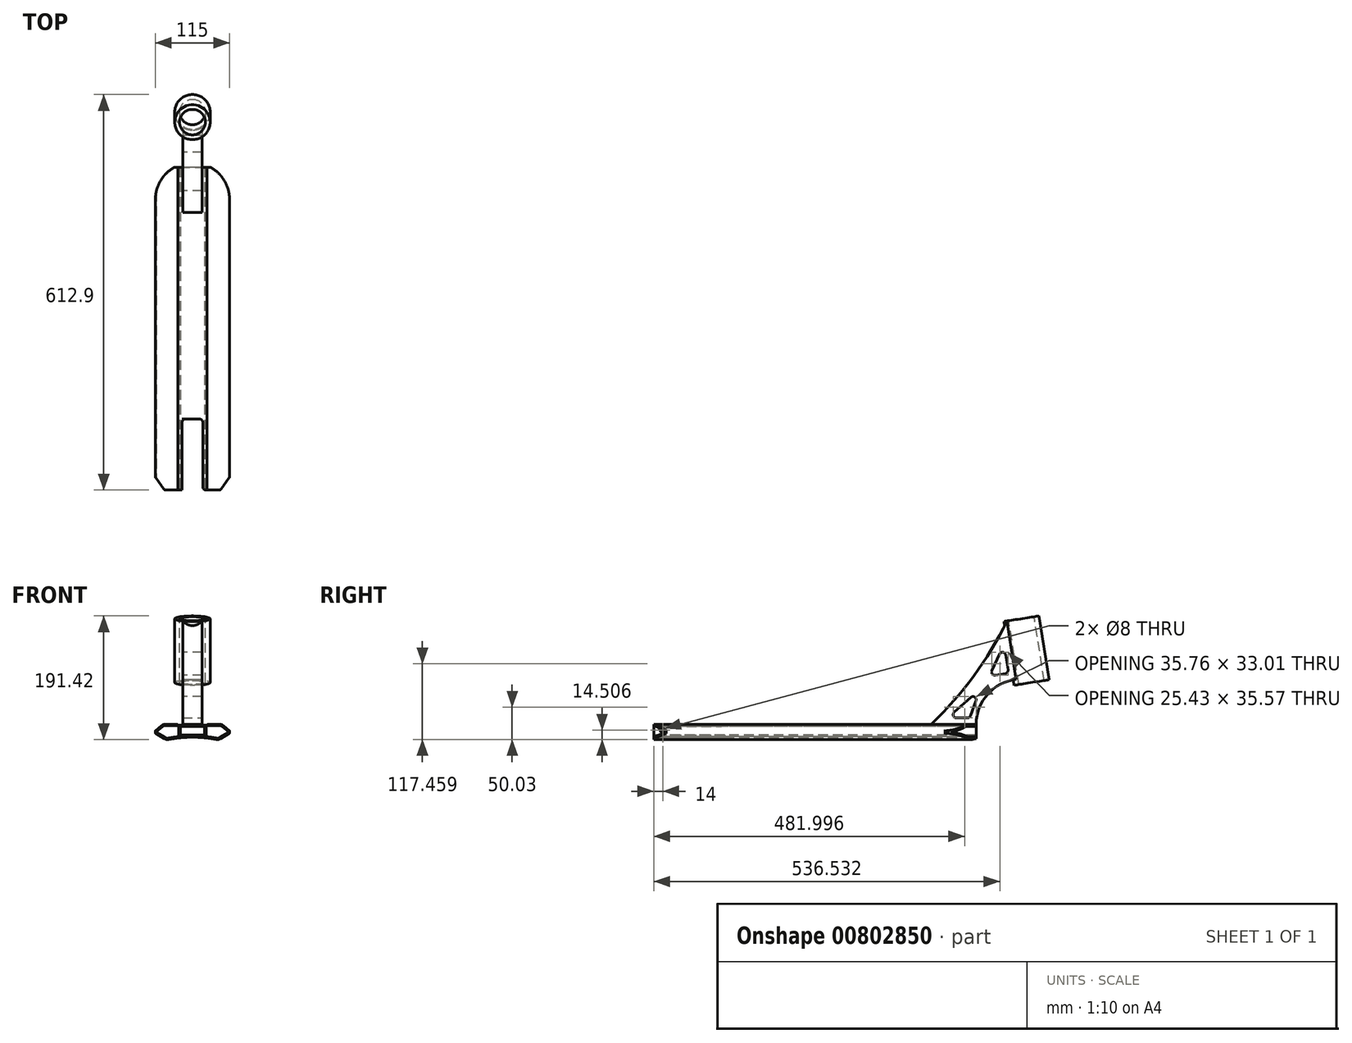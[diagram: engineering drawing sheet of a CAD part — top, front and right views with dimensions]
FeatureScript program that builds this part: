
annotation { "Feature Type Name" : "Feature", "Feature Type Description" : "" }
export const myFeature = defineFeature(function(context is Context, id is Id, definition is map)
    precondition{}
    {
        {
            var Q0;
            Q0=qCreatedBy(makeId("Front.planeOp"),FACE);
            var sketch = newSketch(context, id + "F0", { "sketchPlane" : qUnion([Q0])});
            skLineSegment(sketch, "E0", {"start": v(0, 0) * mm, "end": v(0, 71.95) * mm, "construction": true});
            skLineSegment(sketch, "E1", {"start": v(0, 25.77) * mm, "end": v(22.5, 25.77) * mm});
            skLineSegment(sketch, "E2", {"start": v(22.5, 25.77) * mm, "end": v(22.5, 27.07) * mm});
            skLineSegment(sketch, "E3", {"start": v(22.5, 27.07) * mm, "end": v(45.58, 27.07) * mm});
            skLineSegment(sketch, "E4", {"start": v(45.58, 27.07) * mm, "end": v(57.5, 17.07) * mm});
            skLineSegment(sketch, "E5", {"start": v(57.5, 17.07) * mm, "end": v(57.5, 13.07) * mm});
            skLineSegment(sketch, "E6", {"start": v(57.5, 13.07) * mm, "end": v(40.18, 3.07) * mm});
            skLineSegment(sketch, "E7.MirrorCS", {"start": v(0, 25.77) * mm, "end": v(-22.5, 25.77) * mm});
            skLineSegment(sketch, "E8.MirrorCS", {"start": v(-22.5, 27.07) * mm, "end": v(-45.58, 27.07) * mm});
            skLineSegment(sketch, "E9.MirrorCS", {"start": v(-22.5, 25.77) * mm, "end": v(-22.5, 27.07) * mm});
            skLineSegment(sketch, "E10.MirrorCS", {"start": v(-45.58, 27.07) * mm, "end": v(-57.5, 17.07) * mm});
            skLineSegment(sketch, "E11.MirrorCS", {"start": v(-57.5, 17.07) * mm, "end": v(-57.5, 13.07) * mm});
            skLineSegment(sketch, "E12.MirrorCS", {"start": v(-57.5, 13.07) * mm, "end": v(-40.18, 3.07) * mm});
            skArc(sketch, "E13", {"start": v(40.18, 3.07) * mm, "mid": v(0, 7.15) * mm, "end": v(-40.18, 3.07) * mm});
            skSolve(sketch);
        }
        {
            var Q0;
            Q0=qSketchRegion(id+"F0",true);
            extrude(context, id + "F1", {"entities" : qUnion([Q0]), "endBound" : BoundingType.SYMMETRIC, "depth" : 500 * mm, "offsetDistance" : 25 * mm});
        }
        {
            var Q0;
            Q0=qCreatedBy(makeId("Front.planeOp"),FACE);
            var sketch = newSketch(context, id + "F2", { "sketchPlane" : qUnion([Q0])});
            skLineSegment(sketch, "E14.bottom", {"start": v(-19, 23.77) * mm, "end": v(19, 23.77) * mm});
            skLineSegment(sketch, "E14.top", {"start": v(-19, 10.77) * mm, "end": v(19, 10.77) * mm});
            skLineSegment(sketch, "E14.left", {"start": v(-19, 23.77) * mm, "end": v(-19, 10.77) * mm});
            skLineSegment(sketch, "E14.right", {"start": v(19, 23.77) * mm, "end": v(19, 10.77) * mm});
            skSolve(sketch);
        }
        {
            var Q0;
            Q0=qSketchRegion(id+"F2",true);
            extrude(context, id + "F3", {"entities" : qUnion([Q0]), "operationType" : NewBodyOperationType.REMOVE, "endBound" : BoundingType.SYMMETRIC, "oppositeDirection" : true, "depth" : 500 * mm, "offsetDistance" : 25 * mm});
        }
        {
            var Q0;
            Q0=makeQuery(id+"F1.opExtrude","SWEPT_EDGE",EDGE,{"disambiguationData":[OSD([sQuery(id+"F0.wireOp",EDGE,"E8.MirrorCS"),sQuery(id+"F0.wireOp",EDGE,"E9.MirrorCS")])]});
            var Q1;
            Q1=makeQuery(id+"F1.opExtrude","SWEPT_EDGE",EDGE,{"disambiguationData":[OSD([sQuery(id+"F0.wireOp",EDGE,"E2"),sQuery(id+"F0.wireOp",EDGE,"E3")])]});
            fillet(context, id + "F4", {"entities" : qUnion([Q0, Q1]), "radius" : 2 * mm, "tangentPropagation" : true, "allowEdgeOverflow" : false});
        }
        {
            var Q0;
            Q0=makeQuery(id+"F1.opExtrude","SWEPT_EDGE",EDGE,{"disambiguationData":[OSD([sQuery(id+"F0.wireOp",EDGE,"E8.MirrorCS"),sQuery(id+"F0.wireOp",EDGE,"E10.MirrorCS")])]});
            var Q1;
            Q1=makeQuery(id+"F1.opExtrude","SWEPT_EDGE",EDGE,{"disambiguationData":[OSD([sQuery(id+"F0.wireOp",EDGE,"E3"),sQuery(id+"F0.wireOp",EDGE,"E4")])]});
            var Q2;
            Q2=makeQuery(id+"F1.opExtrude","SWEPT_EDGE",EDGE,{"disambiguationData":[OSD([sQuery(id+"F0.wireOp",EDGE,"E6"),sQuery(id+"F0.wireOp",EDGE,"E13")])]});
            var Q3;
            Q3=makeQuery(id+"F1.opExtrude","SWEPT_EDGE",EDGE,{"disambiguationData":[OSD([sQuery(id+"F0.wireOp",EDGE,"E12.MirrorCS"),sQuery(id+"F0.wireOp",EDGE,"E13")])]});
            fillet(context, id + "F5", {"entities" : qUnion([Q0, Q1, Q2, Q3]), "radius" : 9 * mm, "tangentPropagation" : true, "allowEdgeOverflow" : false});
        }
        {
            var Q0;
            Q0=makeQuery(id+"F1.opExtrude","SWEPT_EDGE",EDGE,{"disambiguationData":[OSD([sQuery(id+"F0.wireOp",EDGE,"E4"),sQuery(id+"F0.wireOp",EDGE,"E5")])]});
            var Q1;
            Q1=makeQuery(id+"F1.opExtrude","SWEPT_EDGE",EDGE,{"disambiguationData":[OSD([sQuery(id+"F0.wireOp",EDGE,"E5"),sQuery(id+"F0.wireOp",EDGE,"E6")])]});
            var Q2;
            Q2=makeQuery(id+"F1.opExtrude","SWEPT_EDGE",EDGE,{"disambiguationData":[OSD([sQuery(id+"F0.wireOp",EDGE,"E10.MirrorCS"),sQuery(id+"F0.wireOp",EDGE,"E11.MirrorCS")])]});
            var Q3;
            Q3=makeQuery(id+"F1.opExtrude","SWEPT_EDGE",EDGE,{"disambiguationData":[OSD([sQuery(id+"F0.wireOp",EDGE,"E11.MirrorCS"),sQuery(id+"F0.wireOp",EDGE,"E12.MirrorCS")])]});
            fillet(context, id + "F6", {"entities" : qUnion([Q0, Q1, Q2, Q3]), "radius" : 1 * mm, "tangentPropagation" : true, "allowEdgeOverflow" : false});
        }
        {
            var Q0;
            Q0=makeQuery(id+"F1.opExtrude","CAP_FACE",FACE,{"disambiguationData":[OSD([sQuery(id+"F0.wireOp",EDGE,"E1"),sQuery(id+"F0.wireOp",EDGE,"E2"),sQuery(id+"F0.wireOp",EDGE,"E3"),sQuery(id+"F0.wireOp",EDGE,"E4"),sQuery(id+"F0.wireOp",EDGE,"E5"),sQuery(id+"F0.wireOp",EDGE,"E6"),sQuery(id+"F0.wireOp",EDGE,"E7.MirrorCS"),sQuery(id+"F0.wireOp",EDGE,"E8.MirrorCS"),sQuery(id+"F0.wireOp",EDGE,"E9.MirrorCS"),sQuery(id+"F0.wireOp",EDGE,"E10.MirrorCS"),sQuery(id+"F0.wireOp",EDGE,"E11.MirrorCS"),sQuery(id+"F0.wireOp",EDGE,"E12.MirrorCS"),sQuery(id+"F0.wireOp",EDGE,"E13")])],"isStart":false});
            var sketch = newSketch(context, id + "F7", { "sketchPlane" : qUnion([Q0])});
            skArc(sketch, "E15.0", {"start": v(-21, 8.06) * mm, "mid": v(-29.18, 7.03) * mm, "end": v(-37.3, 5.68) * mm});
            skArc(sketch, "E15.1", {"start": v(-42.1, 6.5) * mm, "mid": v(-39.78, 5.65) * mm, "end": v(-37.3, 5.68) * mm});
            skLineSegment(sketch, "E15.2", {"start": v(-24.37, 25.07) * mm, "end": v(-42.3, 25.07) * mm});
            skArc(sketch, "E15.3", {"start": v(-42.3, 25.07) * mm, "mid": v(-44.7, 24.65) * mm, "end": v(-46.8, 23.44) * mm});
            skLineSegment(sketch, "E15.4", {"start": v(-46.8, 23.44) * mm, "end": v(-55.76, 15.93) * mm});
            skLineSegment(sketch, "E15.5", {"start": v(-55.61, 14.3) * mm, "end": v(-42.1, 6.5) * mm});
            skLineSegment(sketch, "E16.0", {"start": v(-21, 23.77) * mm, "end": v(-21, 10.77) * mm});
            skLineSegment(sketch, "E17.0", {"start": v(-22.5, 23.77) * mm, "end": v(-21, 23.77) * mm});
            skPoint(sketch, "E18.visualSharp", {"position": v(-56.85, 15) * mm});
            skArc(sketch, "E18.filletArc", {"start": v(-55.76, 15.93) * mm, "mid": v(-56.1, 15.07) * mm, "end": v(-55.61, 14.3) * mm});
            skArc(sketch, "E19", {"start": v(-24.37, 25.07) * mm, "mid": v(-23.23, 24.72) * mm, "end": v(-22.5, 23.77) * mm});
            skLineSegment(sketch, "E20", {"start": v(-21, 10.77) * mm, "end": v(-21, 8.06) * mm});
            skLineSegment(sketch, "E21.MirrorCS", {"start": v(24.37, 25.07) * mm, "end": v(42.3, 25.07) * mm});
            skArc(sketch, "E22.MirrorCS", {"start": v(24.37, 25.07) * mm, "mid": v(23.23, 24.72) * mm, "end": v(22.5, 23.77) * mm});
            skLineSegment(sketch, "E23.MirrorCS", {"start": v(22.5, 23.77) * mm, "end": v(21, 23.77) * mm});
            skLineSegment(sketch, "E24.MirrorCS", {"start": v(21, 23.77) * mm, "end": v(21, 10.77) * mm});
            skArc(sketch, "E25.MirrorCS", {"start": v(21, 8.06) * mm, "mid": v(29.18, 7.03) * mm, "end": v(37.3, 5.68) * mm});
            skArc(sketch, "E26.MirrorCS", {"start": v(42.1, 6.5) * mm, "mid": v(39.78, 5.65) * mm, "end": v(37.3, 5.68) * mm});
            skLineSegment(sketch, "E27.MirrorCS", {"start": v(21, 10.77) * mm, "end": v(21, 8.06) * mm});
            skLineSegment(sketch, "E28.MirrorCS", {"start": v(55.61, 14.3) * mm, "end": v(42.1, 6.5) * mm});
            skLineSegment(sketch, "E29.MirrorCS", {"start": v(46.8, 23.44) * mm, "end": v(55.76, 15.93) * mm});
            skArc(sketch, "E30.MirrorCS", {"start": v(42.3, 25.07) * mm, "mid": v(44.7, 24.65) * mm, "end": v(46.8, 23.44) * mm});
            skArc(sketch, "E31.MirrorCS", {"start": v(55.76, 15.93) * mm, "mid": v(56.1, 15.07) * mm, "end": v(55.61, 14.3) * mm});
            skSolve(sketch);
        }
        {
            var Q0;
            Q0=makeQuery(id+"F7.imprint","IMPRINT",FACE,{"disambiguationData":[TD([[makeQuery(id+"F7.imprint","IMPRINT",EDGE,{"derivedFrom":sQuery(id+"F7.wireOp",EDGE,"E15.0")}),-1.0]])]});
            var Q1;
            Q1=makeQuery(id+"F7.imprint","IMPRINT",FACE,{"disambiguationData":[TD([[makeQuery(id+"F7.imprint","IMPRINT",EDGE,{"derivedFrom":sQuery(id+"F7.wireOp",EDGE,"E21.MirrorCS")}),-1.0]])]});
            extrude(context, id + "F8", {"entities" : qUnion([Q0, Q1]), "operationType" : NewBodyOperationType.REMOVE, "endBound" : BoundingType.THROUGH_ALL, "oppositeDirection" : true, "depth" : 25 * mm, "offsetDistance" : 25 * mm});
        }
        {
            var Q0;
            Q0=qCreatedBy(makeId("Top.planeOp"),FACE);
            var sketch = newSketch(context, id + "F9", { "sketchPlane" : qUnion([Q0])});
            skArc(sketch, "E32", {"start": v(57.5, 200) * mm, "mid": v(0, 257.5) * mm, "end": v(-57.5, 200) * mm});
            skLineSegment(sketch, "E33", {"start": v(-57.5, 280) * mm, "end": v(-57.5, 200) * mm});
            skLineSegment(sketch, "E34", {"start": v(57.5, 200) * mm, "end": v(57.5, 280) * mm});
            skLineSegment(sketch, "E35", {"start": v(-57.5, 280) * mm, "end": v(57.5, 280) * mm});
            skSolve(sketch);
        }
        {
            var Q0;
            Q0=qSketchRegion(id+"F9",true);
            extrude(context, id + "F10", {"entities" : qUnion([Q0]), "operationType" : NewBodyOperationType.REMOVE, "endBound" : BoundingType.THROUGH_ALL, "oppositeDirection" : true, "depth" : 25 * mm, "offsetDistance" : 25 * mm, "hasSecondDirection" : true, "secondDirectionBound" : SecondDirectionBoundingType.THROUGH_ALL, "secondDirectionOppositeDirection" : false, "secondDirectionDepth" : 25 * mm});
        }
        {
            var Q0;
            Q0=qCreatedBy(makeId("Top.planeOp"),FACE);
            var sketch = newSketch(context, id + "F11", { "sketchPlane" : qUnion([Q0])});
            skLineSegment(sketch, "E36", {"start": v(-68, -216) * mm, "end": v(-68, -346) * mm});
            skLineSegment(sketch, "E37", {"start": v(-68, -346) * mm, "end": v(68, -346) * mm});
            skLineSegment(sketch, "E38", {"start": v(68, -346) * mm, "end": v(68, -216) * mm});
            skLineSegment(sketch, "E39", {"start": v(68, -216) * mm, "end": v(43.3, -250) * mm});
            skLineSegment(sketch, "E40", {"start": v(43.3, -250) * mm, "end": v(16, -250) * mm});
            skLineSegment(sketch, "E41", {"start": v(16, -250) * mm, "end": v(16, -140) * mm});
            skLineSegment(sketch, "E42", {"start": v(16, -140) * mm, "end": v(-16, -140) * mm});
            skLineSegment(sketch, "E43", {"start": v(-16, -140) * mm, "end": v(-16, -250) * mm});
            skLineSegment(sketch, "E44", {"start": v(-16, -250) * mm, "end": v(-43.3, -250) * mm});
            skLineSegment(sketch, "E45", {"start": v(-43.3, -250) * mm, "end": v(-68, -216) * mm});
            skSolve(sketch);
        }
        {
            var Q0;
            Q0=qSketchRegion(id+"F11",true);
            extrude(context, id + "F12", {"entities" : qUnion([Q0]), "operationType" : NewBodyOperationType.REMOVE, "endBound" : BoundingType.THROUGH_ALL, "depth" : 25 * mm, "offsetDistance" : 25 * mm, "hasSecondDirection" : true, "secondDirectionBound" : SecondDirectionBoundingType.THROUGH_ALL, "secondDirectionOppositeDirection" : true, "secondDirectionDepth" : 25 * mm});
        }
        {
            var Q0;
            {var subQ0=sQuery(id+"F0.wireOp",EDGE,"E13");var subQ1=sQuery(id+"F11.wireOp",EDGE,"E43");Q0=makeQuery(id+"F12.boolean.opBoolean","COPY",EDGE,{"disambiguationData":[TD([makeQuery(id+"F1.opExtrude","SWEPT_FACE",FACE,{"disambiguationData":[OSD([subQ0])]})])],"derivedFrom":makeQuery(id+"F12.opExtrude","SWEPT_EDGE",EDGE,{"disambiguationData":[OSD([subQ1,sQuery(id+"F11.wireOp",EDGE,"E44")])]})});}
            var Q1;
            {var subQ2=sQuery(id+"F11.wireOp",EDGE,"E43");Q1=makeQuery(id+"F12.boolean.opBoolean","COPY",EDGE,{"disambiguationData":[TD([makeQuery(id+"F3.boolean.opBoolean","COPY",FACE,{"derivedFrom":makeQuery(id+"F3.opExtrude","SWEPT_FACE",FACE,{"disambiguationData":[OSD([sQuery(id+"F2.wireOp",EDGE,"E14.bottom")])]})})])],"derivedFrom":makeQuery(id+"F12.opExtrude","SWEPT_EDGE",EDGE,{"disambiguationData":[OSD([subQ2,sQuery(id+"F11.wireOp",EDGE,"E44")])]})});}
            var Q2;
            {var subQ0=sQuery(id+"F11.wireOp",EDGE,"E42");var subQ1=sQuery(id+"F11.wireOp",EDGE,"E43");Q2=makeQuery(id+"F12.boolean.opBoolean","COPY",EDGE,{"disambiguationData":[TD([makeQuery(id+"F3.boolean.opBoolean","COPY",FACE,{"derivedFrom":makeQuery(id+"F3.opExtrude","SWEPT_FACE",FACE,{"disambiguationData":[OSD([sQuery(id+"F2.wireOp",EDGE,"E14.bottom")])]})})])],"derivedFrom":makeQuery(id+"F12.opExtrude","SWEPT_EDGE",EDGE,{"disambiguationData":[OSD([subQ0,subQ1])]})});}
            var Q3;
            {var subQ0=sQuery(id+"F11.wireOp",EDGE,"E41");var subQ1=sQuery(id+"F11.wireOp",EDGE,"E42");Q3=makeQuery(id+"F12.boolean.opBoolean","COPY",EDGE,{"disambiguationData":[TD([makeQuery(id+"F1.opExtrude","SWEPT_FACE",FACE,{"disambiguationData":[OSD([sQuery(id+"F0.wireOp",EDGE,"E13")])]})])],"derivedFrom":makeQuery(id+"F12.opExtrude","SWEPT_EDGE",EDGE,{"disambiguationData":[OSD([subQ0,subQ1])]})});}
            var Q4;
            {var subQ0=sQuery(id+"F0.wireOp",EDGE,"E13");var subQ1=sQuery(id+"F11.wireOp",EDGE,"E41");Q4=makeQuery(id+"F12.boolean.opBoolean","COPY",EDGE,{"disambiguationData":[TD([makeQuery(id+"F1.opExtrude","SWEPT_FACE",FACE,{"disambiguationData":[OSD([subQ0])]})])],"derivedFrom":makeQuery(id+"F12.opExtrude","SWEPT_EDGE",EDGE,{"disambiguationData":[OSD([sQuery(id+"F11.wireOp",EDGE,"E40"),subQ1])]})});}
            var Q5;
            {var subQ2=sQuery(id+"F11.wireOp",EDGE,"E41");Q5=makeQuery(id+"F12.boolean.opBoolean","COPY",EDGE,{"disambiguationData":[TD([makeQuery(id+"F3.boolean.opBoolean","COPY",FACE,{"derivedFrom":makeQuery(id+"F3.opExtrude","SWEPT_FACE",FACE,{"disambiguationData":[OSD([sQuery(id+"F2.wireOp",EDGE,"E14.bottom")])]})})])],"derivedFrom":makeQuery(id+"F12.opExtrude","SWEPT_EDGE",EDGE,{"disambiguationData":[OSD([sQuery(id+"F11.wireOp",EDGE,"E40"),subQ2])]})});}
            var Q6;
            {var subQ0=sQuery(id+"F11.wireOp",EDGE,"E42");var subQ1=sQuery(id+"F11.wireOp",EDGE,"E41");Q6=makeQuery(id+"F12.boolean.opBoolean","COPY",EDGE,{"disambiguationData":[TD([makeQuery(id+"F3.boolean.opBoolean","COPY",FACE,{"derivedFrom":makeQuery(id+"F3.opExtrude","SWEPT_FACE",FACE,{"disambiguationData":[OSD([sQuery(id+"F2.wireOp",EDGE,"E14.bottom")])]})})])],"derivedFrom":makeQuery(id+"F12.opExtrude","SWEPT_EDGE",EDGE,{"disambiguationData":[OSD([subQ1,subQ0])]})});}
            fillet(context, id + "F13", {"entities" : qUnion([Q0, Q1, Q2, Q3, Q4, Q5, Q6]), "radius" : 5 * mm, "tangentPropagation" : true, "allowEdgeOverflow" : false});
        }
        {
            var Q0;
            Q0=qCreatedBy(makeId("Right.planeOp"),FACE);
            var sketch = newSketch(context, id + "F14", { "sketchPlane" : qUnion([Q0])});
            skLineSegment(sketch, "E46", {"start": v(250, 27.07) * mm, "end": v(180, 27.07) * mm});
            skArc(sketch, "E47", {"start": v(311.71, 96.58) * mm, "mid": v(267.66, 73.55) * mm, "end": v(250, 27.07) * mm});
            skArc(sketch, "E48", {"start": v(180, 27.07) * mm, "mid": v(245.97, 101.74) * mm, "end": v(297.38, 187.07) * mm});
            skLineSegment(sketch, "E49", {"start": v(297.38, 187.07) * mm, "end": v(342.82, 194.27) * mm});
            skLineSegment(sketch, "E50", {"start": v(342.82, 194.27) * mm, "end": v(358.46, 95.5) * mm});
            skLineSegment(sketch, "E51", {"start": v(358.46, 95.5) * mm, "end": v(313.03, 88.3) * mm});
            skLineSegment(sketch, "E52", {"start": v(313.03, 88.3) * mm, "end": v(311.71, 96.58) * mm});
            skSolve(sketch);
        }
        {
            var Q0;
            Q0=qSketchRegion(id+"F14",true);
            extrude(context, id + "F15", {"entities" : qUnion([Q0]), "endBound" : BoundingType.SYMMETRIC, "depth" : 30 * mm, "offsetDistance" : 25 * mm});
        }
        {
            var Q0;
            Q0=makeQuery(id+"F15.opExtrude","SWEPT_FACE",FACE,{"disambiguationData":[OSD([sQuery(id+"F14.wireOp",EDGE,"E49")])]});
            var sketch = newSketch(context, id + "F16", { "sketchPlane" : qUnion([Q0])});
            skCircle(sketch, "E53", {"center": v(0, 345.99) * mm, "radius": 27.5 * mm});
            skPoint(sketch, "E53.centerSnap0", {"position": v(15, 345.99) * mm});
            skSolve(sketch);
        }
        {
            var Q0;
            Q0=qSketchRegion(id+"F16",true);
            var Q1;
            Q1=makeQuery(id+"F15.opExtrude","SWEPT_FACE",FACE,{"disambiguationData":[OSD([sQuery(id+"F14.wireOp",EDGE,"E51")])]});
            extrude(context, id + "F17", {"entities" : qUnion([Q0]), "operationType" : NewBodyOperationType.ADD, "endBound" : BoundingType.UP_TO_SURFACE, "oppositeDirection" : true, "depth" : 25 * mm, "endBoundEntityFace" : qUnion([Q1]), "offsetDistance" : 25 * mm});
        }
        {
            var Q0;
            Q0=makeQuery(id+"F17.boolean.opBoolean","MERGE",FACE,{"derivedFrom":[makeQuery(id+"F15.opExtrude","SWEPT_FACE",FACE,{"disambiguationData":[OSD([sQuery(id+"F14.wireOp",EDGE,"E49")])]}),makeQuery(id+"F17.opExtrude","CAP_FACE",FACE,{"disambiguationData":[OSD([sQuery(id+"F16.wireOp",EDGE,"E53")])],"isStart":true})]});
            var sketch = newSketch(context, id + "F18", { "sketchPlane" : qUnion([Q0])});
            skPoint(sketch, "E54", {"position": v(0, 345.99) * mm});
            skSolve(sketch);
        }
        {
            var Q0;
            Q0=sQuery(id+"F18.wireOp",VERTEX,"E54");
            var Q1;
            Q1=makeQuery(id+"F15.opExtrude","SWEPT_BODY",BODY,{"disambiguationData":[OSD([sQuery(id+"F14.wireOp",EDGE,"E46"),sQuery(id+"F14.wireOp",EDGE,"E47"),sQuery(id+"F14.wireOp",EDGE,"E48"),sQuery(id+"F14.wireOp",EDGE,"E49"),sQuery(id+"F14.wireOp",EDGE,"E50"),sQuery(id+"F14.wireOp",EDGE,"E51"),sQuery(id+"F14.wireOp",EDGE,"E52")])]});
            hole(context, id + "F19", {"style" : HoleStyle.SIMPLE, "endStyle" : HoleEndStyle.THROUGH, "holeDiameter" : 40 * mm, "majorDiameter" : 5 * mm, "isTappedThrough" : true, "tappedDepth" : 12 * mm, "tapClearance" : 3, "locations" : qUnion([Q0]), "scope" : qUnion([Q1])});
        }
        {
            var Q0;
            Q0=makeQuery(id+"F8.boolean.opBoolean","COPY",FACE,{"derivedFrom":makeQuery(id+"F8.opExtrude","SWEPT_FACE",FACE,{"disambiguationData":[OSD([sQuery(id+"F7.wireOp",EDGE,"E24.MirrorCS"),sQuery(id+"F7.wireOp",EDGE,"E27.MirrorCS")])]})});
            var sketch = newSketch(context, id + "F20", { "sketchPlane" : qUnion([Q0])});
            skPoint(sketch, "E55", {"position": v(-236, 18.06) * mm});
            skSolve(sketch);
        }
        {
            var Q0;
            Q0=sQuery(id+"F20.wireOp",VERTEX,"E55");
            var Q1;
            Q1=makeQuery(id+"F1.opExtrude","SWEPT_BODY",BODY,{"disambiguationData":[OSD([sQuery(id+"F0.wireOp",EDGE,"E1"),sQuery(id+"F0.wireOp",EDGE,"E2"),sQuery(id+"F0.wireOp",EDGE,"E3"),sQuery(id+"F0.wireOp",EDGE,"E4"),sQuery(id+"F0.wireOp",EDGE,"E5"),sQuery(id+"F0.wireOp",EDGE,"E6"),sQuery(id+"F0.wireOp",EDGE,"E7.MirrorCS"),sQuery(id+"F0.wireOp",EDGE,"E8.MirrorCS"),sQuery(id+"F0.wireOp",EDGE,"E9.MirrorCS"),sQuery(id+"F0.wireOp",EDGE,"E10.MirrorCS"),sQuery(id+"F0.wireOp",EDGE,"E11.MirrorCS"),sQuery(id+"F0.wireOp",EDGE,"E12.MirrorCS"),sQuery(id+"F0.wireOp",EDGE,"E13")])]});
            hole(context, id + "F21", {"style" : HoleStyle.SIMPLE, "endStyle" : HoleEndStyle.BLIND, "holeDiameter" : 8 * mm, "majorDiameter" : 5 * mm, "holeDepth" : 66 * mm, "isTappedThrough" : true, "tappedDepth" : 12 * mm, "tapClearance" : 3, "locations" : qUnion([Q0]), "scope" : qUnion([Q1])});
        }
        {
            var Q0;
            Q0=makeQuery(id+"F15.opExtrude","CAP_FACE",FACE,{"disambiguationData":[OSD([sQuery(id+"F14.wireOp",EDGE,"E46"),sQuery(id+"F14.wireOp",EDGE,"E47"),sQuery(id+"F14.wireOp",EDGE,"E48"),sQuery(id+"F14.wireOp",EDGE,"E49"),sQuery(id+"F14.wireOp",EDGE,"E50"),sQuery(id+"F14.wireOp",EDGE,"E51"),sQuery(id+"F14.wireOp",EDGE,"E52")])],"isStart":false});
            var sketch = newSketch(context, id + "F22", { "sketchPlane" : qUnion([Q0])});
            skLineSegment(sketch, "E56", {"start": v(206, 37.07) * mm, "end": v(240, 37.07) * mm});
            skLineSegment(sketch, "E57", {"start": v(240, 37.07) * mm, "end": v(256.38, 82.07) * mm});
            skLineSegment(sketch, "E58", {"start": v(256.38, 82.07) * mm, "end": v(206, 37.07) * mm});
            skLineSegment(sketch, "E59", {"start": v(270.34, 101.8) * mm, "end": v(299.97, 106.49) * mm});
            skLineSegment(sketch, "E60", {"start": v(299.97, 106.49) * mm, "end": v(292.93, 150.93) * mm});
            skLineSegment(sketch, "E61", {"start": v(292.93, 150.93) * mm, "end": v(270.34, 101.8) * mm});
            skSolve(sketch);
        }
        {
            var Q0;
            Q0=qSketchRegion(id+"F22",true);
            extrude(context, id + "F23", {"entities" : qUnion([Q0]), "operationType" : NewBodyOperationType.REMOVE, "endBound" : BoundingType.THROUGH_ALL, "oppositeDirection" : true, "depth" : 25 * mm, "offsetDistance" : 25 * mm});
        }
        {
            var Q0;
            Q0=makeQuery(id+"F23.boolean.opBoolean","COPY",EDGE,{"derivedFrom":makeQuery(id+"F23.opExtrude","SWEPT_EDGE",EDGE,{"disambiguationData":[OSD([sQuery(id+"F22.wireOp",EDGE,"E60"),sQuery(id+"F22.wireOp",EDGE,"E61")])]})});
            var Q1;
            Q1=makeQuery(id+"F23.boolean.opBoolean","COPY",EDGE,{"derivedFrom":makeQuery(id+"F23.opExtrude","SWEPT_EDGE",EDGE,{"disambiguationData":[OSD([sQuery(id+"F22.wireOp",EDGE,"E59"),sQuery(id+"F22.wireOp",EDGE,"E61")])]})});
            var Q2;
            Q2=makeQuery(id+"F23.boolean.opBoolean","COPY",EDGE,{"derivedFrom":makeQuery(id+"F23.opExtrude","SWEPT_EDGE",EDGE,{"disambiguationData":[OSD([sQuery(id+"F22.wireOp",EDGE,"E59"),sQuery(id+"F22.wireOp",EDGE,"E60")])]})});
            var Q3;
            Q3=makeQuery(id+"F23.boolean.opBoolean","COPY",EDGE,{"derivedFrom":makeQuery(id+"F23.opExtrude","SWEPT_EDGE",EDGE,{"disambiguationData":[OSD([sQuery(id+"F22.wireOp",EDGE,"E56"),sQuery(id+"F22.wireOp",EDGE,"E57")])]})});
            var Q4;
            Q4=makeQuery(id+"F23.boolean.opBoolean","COPY",EDGE,{"derivedFrom":makeQuery(id+"F23.opExtrude","SWEPT_EDGE",EDGE,{"disambiguationData":[OSD([sQuery(id+"F22.wireOp",EDGE,"E57"),sQuery(id+"F22.wireOp",EDGE,"E58")])]})});
            var Q5;
            Q5=makeQuery(id+"F23.boolean.opBoolean","COPY",EDGE,{"derivedFrom":makeQuery(id+"F23.opExtrude","SWEPT_EDGE",EDGE,{"disambiguationData":[OSD([sQuery(id+"F22.wireOp",EDGE,"E56"),sQuery(id+"F22.wireOp",EDGE,"E58")])]})});
            fillet(context, id + "F24", {"entities" : qUnion([Q0, Q1, Q2, Q3, Q4, Q5]), "radius" : 5 * mm, "tangentPropagation" : true, "allowEdgeOverflow" : false});
        }
    });
